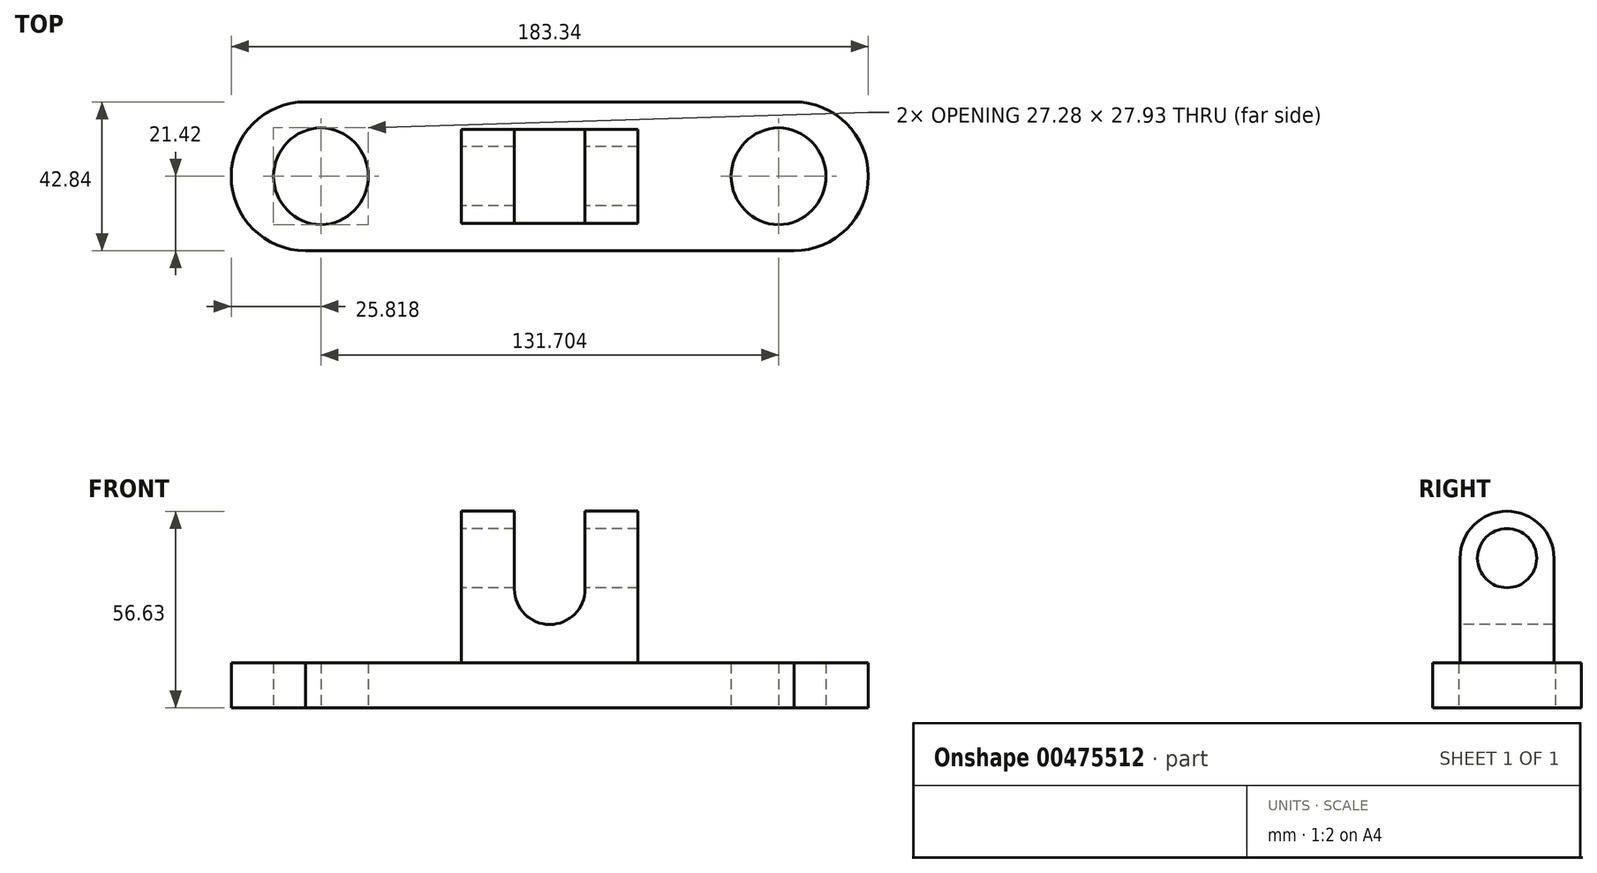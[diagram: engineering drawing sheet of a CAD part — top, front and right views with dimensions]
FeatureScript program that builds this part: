
annotation { "Feature Type Name" : "Feature", "Feature Type Description" : "" }
export const myFeature = defineFeature(function(context is Context, id is Id, definition is map)
    precondition{}
    {
        {
            var Q0;
            Q0=qCreatedBy(makeId("Top.planeOp"),FACE);
            var sketch = newSketch(context, id + "F0", { "sketchPlane" : qUnion([Q0])});
            skLineSegment(sketch, "E0.bottom", {"start": v(70.25, 21.4) * mm, "end": v(-70.25, 21.4) * mm});
            skLineSegment(sketch, "E0.top", {"start": v(70.25, -21.4) * mm, "end": v(-70.25, -21.4) * mm});
            skLineSegment(sketch, "E0.left", {"start": v(70.25, 21.4) * mm, "end": v(70.25, 21.23) * mm});
            skLineSegment(sketch, "E0.right", {"start": v(-70.25, 21.42) * mm, "end": v(-70.25, 21.4) * mm});
            skPoint(sketch, "E0.middle", {"position": v(0, 0) * mm});
            skArc(sketch, "E1", {"start": v(-70.25, 21.42) * mm, "mid": v(-91.67, 0) * mm, "end": v(-70.25, -21.42) * mm});
            skArc(sketch, "E2", {"start": v(70.25, -21.23) * mm, "mid": v(91.49, 0) * mm, "end": v(70.25, 21.23) * mm});
            skLineSegment(sketch, "E3.trimOffspring", {"start": v(-70.25, -21.4) * mm, "end": v(-70.25, -21.42) * mm});
            skPoint(sketch, "E4.orphan", {"position": v(-70.25, 27) * mm});
            skLineSegment(sketch, "E5.trimOffspring", {"start": v(70.25, -21.23) * mm, "end": v(70.25, -21.4) * mm});
            skSolve(sketch);
        }
        {
            var Q0;
            Q0=makeQuery(id+"F0.imprint","IMPRINT",FACE,{"disambiguationData":[TD([[makeQuery(id+"F0.imprint","IMPRINT",EDGE,{"derivedFrom":sQuery(id+"F0.wireOp",EDGE,"E0.bottom")}),1.0]])]});
            extrude(context, id + "F1", {"entities" : qUnion([Q0]), "depth" : 12.95 * mm});
        }
        {
            var Q0;
            Q0=qCreatedBy(makeId("Top.planeOp"),FACE);
            var sketch = newSketch(context, id + "F2", { "sketchPlane" : qUnion([Q0])});
            skCircle(sketch, "E6", {"center": v(-65.52, 0) * mm, "radius": 14.52 * mm});
            skCircle(sketch, "E7", {"center": v(66.18, 0) * mm, "radius": 14.46 * mm});
            skSolve(sketch);
        }
        {
            var Q0;
            Q0=sQuery(id+"F2.wireOp",VERTEX,"E6.center");
            var Q1;
            Q1=sQuery(id+"F2.wireOp",VERTEX,"E7.center");
            var Q2;
            Q2=makeQuery(id+"F1.opExtrude","SWEPT_BODY",BODY,{"disambiguationData":[OSD([sQuery(id+"F0.wireOp",EDGE,"E0.bottom"),sQuery(id+"F0.wireOp",EDGE,"E0.top"),sQuery(id+"F0.wireOp",EDGE,"E0.left"),sQuery(id+"F0.wireOp",EDGE,"E1"),sQuery(id+"F0.wireOp",EDGE,"E2"),sQuery(id+"F0.wireOp",EDGE,"E0.right"),sQuery(id+"F0.wireOp",EDGE,"E3.trimOffspring"),sQuery(id+"F0.wireOp",EDGE,"E5.trimOffspring")])]});
            hole(context, id + "F3", {"style" : HoleStyle.SIMPLE, "endStyle" : HoleEndStyle.BLIND, "oppositeDirection" : true, "holeDiameter" : 27.94 * mm, "holeDepth" : 20.32 * mm, "isTappedThrough" : true, "tappedDepth" : 12.7 * mm, "tapClearance" : 3, "locations" : qUnion([Q0, Q1]), "scope" : qUnion([Q2])});
        }
        {
            var Q0;
            Q0=qCreatedBy(makeId("Right.planeOp"),FACE);
            var sketch = newSketch(context, id + "F4", { "sketchPlane" : qUnion([Q0])});
            skLineSegment(sketch, "E8.top", {"start": v(13.5, 7.57) * mm, "end": v(-13.5, 7.57) * mm});
            skLineSegment(sketch, "E8.left", {"start": v(13.5, 43.13) * mm, "end": v(13.5, 7.57) * mm});
            skLineSegment(sketch, "E8.right", {"start": v(-13.5, 43.13) * mm, "end": v(-13.5, 7.57) * mm});
            skPoint(sketch, "E8.middle", {"position": v(0, 25.35) * mm});
            skArc(sketch, "E9", {"start": v(13.5, 43.13) * mm, "mid": v(0, 56.63) * mm, "end": v(-13.5, 43.13) * mm});
            skSolve(sketch);
        }
        {
            var Q0;
            Q0=makeQuery(id+"F4.imprint","IMPRINT",FACE,{"disambiguationData":[TD([[makeQuery(id+"F4.imprint","IMPRINT",EDGE,{"derivedFrom":sQuery(id+"F4.wireOp",EDGE,"E8.top")}),-1.0]])]});
            extrude(context, id + "F5", {"entities" : qUnion([Q0]), "operationType" : NewBodyOperationType.ADD, "depth" : 25.4 * mm});
        }
        {
            var Q0;
            Q0=makeQuery(id+"F1.opExtrude","SWEPT_BODY",BODY,{"disambiguationData":[OSD([sQuery(id+"F0.wireOp",EDGE,"E0.bottom"),sQuery(id+"F0.wireOp",EDGE,"E0.top"),sQuery(id+"F0.wireOp",EDGE,"E0.left"),sQuery(id+"F0.wireOp",EDGE,"E1"),sQuery(id+"F0.wireOp",EDGE,"E2"),sQuery(id+"F0.wireOp",EDGE,"E0.right"),sQuery(id+"F0.wireOp",EDGE,"E3.trimOffspring"),sQuery(id+"F0.wireOp",EDGE,"E5.trimOffspring")])]});
            var Q1;
            Q1=makeQuery(id+"F5.opExtrude","CAP_FACE",FACE,{"disambiguationData":[OSD([sQuery(id+"F4.wireOp",EDGE,"E8.top"),sQuery(id+"F4.wireOp",EDGE,"E8.left"),sQuery(id+"F4.wireOp",EDGE,"E8.right"),sQuery(id+"F4.wireOp",EDGE,"E9")])],"isStart":true});
            mirror(context, id + "F6", {"operationType" : NewBodyOperationType.ADD, "entities" : qUnion([Q0]), "mirrorPlane" : qUnion([Q1])});
        }
        {
            var Q0;
            {var subQ0=makeQuery(id+"F5.opExtrude","SWEPT_FACE",FACE,{"disambiguationData":[OSD([sQuery(id+"F4.wireOp",EDGE,"E8.right")])]});Q0=makeQuery(id+"F6.boolean.opBoolean","MERGE",FACE,{"derivedFrom":[subQ0,makeQuery(id+"F6.opPattern","COPY",FACE,{"derivedFrom":subQ0,"instanceName":"1"})]});}
            var sketch = newSketch(context, id + "F7", { "sketchPlane" : qUnion([Q0])});
            skLineSegment(sketch, "E10", {"start": v(-10.16, 43.13) * mm, "end": v(-10.16, 59.45) * mm});
            skLineSegment(sketch, "E11", {"start": v(-10.16, 59.45) * mm, "end": v(10.16, 59.45) * mm});
            skLineSegment(sketch, "E12", {"start": v(10.16, 59.45) * mm, "end": v(10.16, 43.13) * mm});
            skLineSegment(sketch, "E13", {"start": v(10.16, 34.2) * mm, "end": v(-10.16, 34.2) * mm});
            skLineSegment(sketch, "E14", {"start": v(-10.16, 34.2) * mm, "end": v(-10.16, 43.13) * mm});
            skLineSegment(sketch, "E15", {"start": v(10.16, 43.13) * mm, "end": v(10.16, 34.2) * mm});
            skArc(sketch, "E16", {"start": v(10.16, 34.2) * mm, "mid": v(0, 24.04) * mm, "end": v(-10.16, 34.2) * mm});
            skSolve(sketch);
        }
        {
            var Q0;
            Q0 = qSketchRegion(id + "F7", true);
            extrude(context, id + "F8", {"entities" : qUnion([Q0]), "operationType" : NewBodyOperationType.REMOVE, "endBound" : BoundingType.THROUGH_ALL, "oppositeDirection" : true, "depth" : 25.4 * mm});
        }
        {
            var Q0;
            Q0=makeQuery(id+"F6.opPattern","COPY",FACE,{"derivedFrom":makeQuery(id+"F5.opExtrude","CAP_FACE",FACE,{"disambiguationData":[OSD([sQuery(id+"F4.wireOp",EDGE,"E8.top"),sQuery(id+"F4.wireOp",EDGE,"E8.left"),sQuery(id+"F4.wireOp",EDGE,"E8.right"),sQuery(id+"F4.wireOp",EDGE,"E9")])],"isStart":false}),"instanceName":"1"});
            var sketch = newSketch(context, id + "F9", { "sketchPlane" : qUnion([Q0])});
            skCircle(sketch, "E17", {"center": v(0, 43.13) * mm, "radius": 8.51 * mm});
            skSolve(sketch);
        }
        {
            var Q0;
            Q0 = qSketchRegion(id + "F9", true);
            extrude(context, id + "F10", {"entities" : qUnion([Q0]), "operationType" : NewBodyOperationType.REMOVE, "endBound" : BoundingType.THROUGH_ALL, "oppositeDirection" : true, "depth" : 25.4 * mm});
        }
    });
